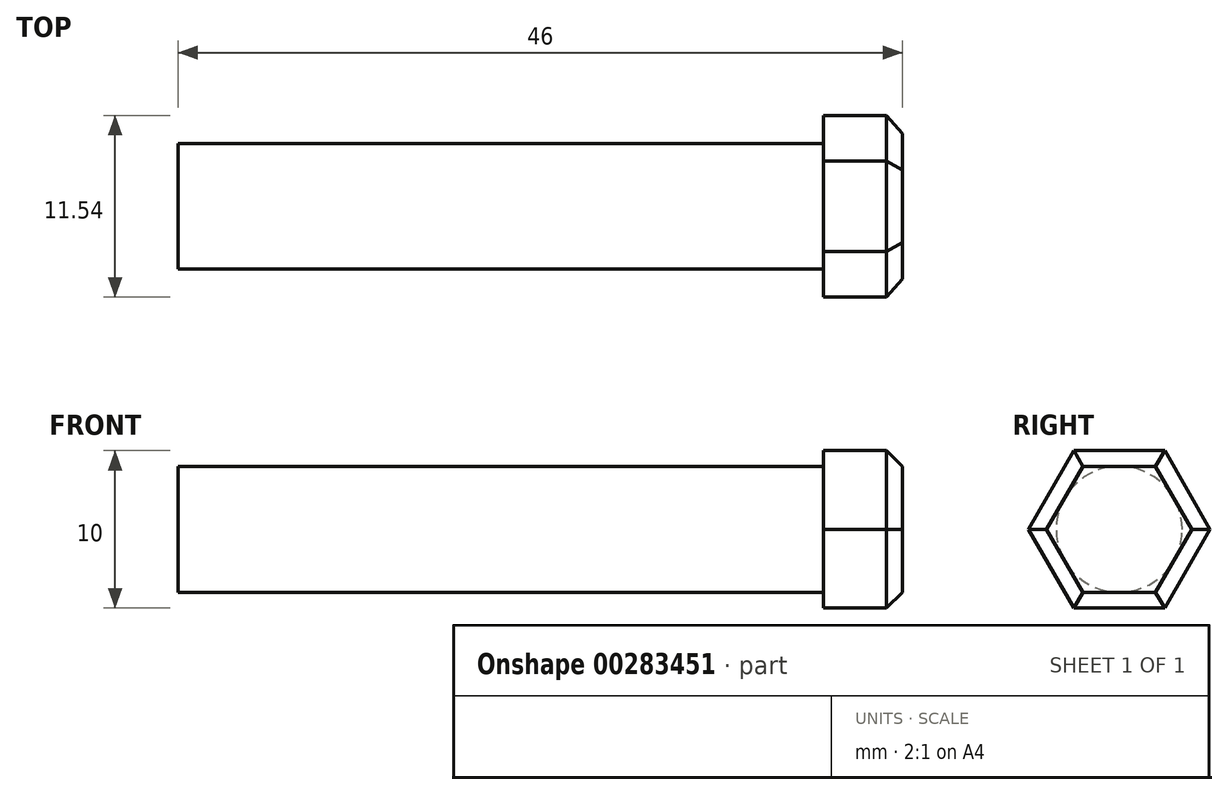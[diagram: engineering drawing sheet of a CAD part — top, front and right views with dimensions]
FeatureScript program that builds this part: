
annotation { "Feature Type Name" : "Feature", "Feature Type Description" : "" }
export const myFeature = defineFeature(function(context is Context, id is Id, definition is map)
    precondition{}
    {
        {
            var Q0;
            Q0=qCreatedBy(makeId("Right.planeOp"),FACE);
            var sketch = newSketch(context, id + "F0", { "sketchPlane" : qUnion([Q0])});
            skCircle(sketch, "E0", {"center": v(0, 0) * mm, "radius": 4 * mm});
            skSolve(sketch);
        }
        {
            var Q0;
            Q0 = qSketchRegion(id + "F0", true);
            extrude(context, id + "F1", {"entities" : qUnion([Q0]), "endBound" : BoundingType.SYMMETRIC, "depth" : 41 * mm});
        }
        {
            var Q0;
            Q0=makeQuery(id+"F1.opExtrude","CAP_FACE",FACE,{"disambiguationData":[OSD([sQuery(id+"F0.wireOp",EDGE,"E0")])],"isStart":false});
            var sketch = newSketch(context, id + "F2", { "sketchPlane" : qUnion([Q0])});
            skCircle(sketch, "E1.cCircle", {"center": v(0, 0) * mm, "radius": 5 * mm, "construction": true});
            skLineSegment(sketch, "E1.0", {"start": v(-2.89, 5) * mm, "end": v(2.89, 5) * mm});
            skLineSegment(sketch, "E1.1", {"start": v(2.89, 5) * mm, "end": v(5.77, 0) * mm});
            skLineSegment(sketch, "E1.2", {"start": v(5.77, 0) * mm, "end": v(2.89, -5) * mm});
            skLineSegment(sketch, "E1.3", {"start": v(2.89, -5) * mm, "end": v(-2.89, -5) * mm});
            skLineSegment(sketch, "E1.4", {"start": v(-2.89, -5) * mm, "end": v(-5.77, 0) * mm});
            skLineSegment(sketch, "E1.5", {"start": v(-5.77, 0) * mm, "end": v(-2.89, 5) * mm});
            skPoint(sketch, "E1.0.midPoint", {"position": v(0, 5) * mm});
            skSolve(sketch);
        }
        {
            var Q0;
            Q0 = qSketchRegion(id + "F2", true);
            extrude(context, id + "F3", {"entities" : qUnion([Q0]), "operationType" : NewBodyOperationType.ADD, "depth" : 5 * mm});
        }
        {
            var Q0;
            Q0=makeQuery(id+"F3.opExtrude","CAP_FACE",FACE,{"disambiguationData":[OSD([sQuery(id+"F2.wireOp",EDGE,"E1.0"),sQuery(id+"F2.wireOp",EDGE,"E1.1"),sQuery(id+"F2.wireOp",EDGE,"E1.2"),sQuery(id+"F2.wireOp",EDGE,"E1.3"),sQuery(id+"F2.wireOp",EDGE,"E1.4"),sQuery(id+"F2.wireOp",EDGE,"E1.5")])],"isStart":false});
            chamfer(context, id + "F4", {"entities" : qUnion([Q0]), "width" : 1 * mm, "tangentPropagation" : true});
        }
    });
